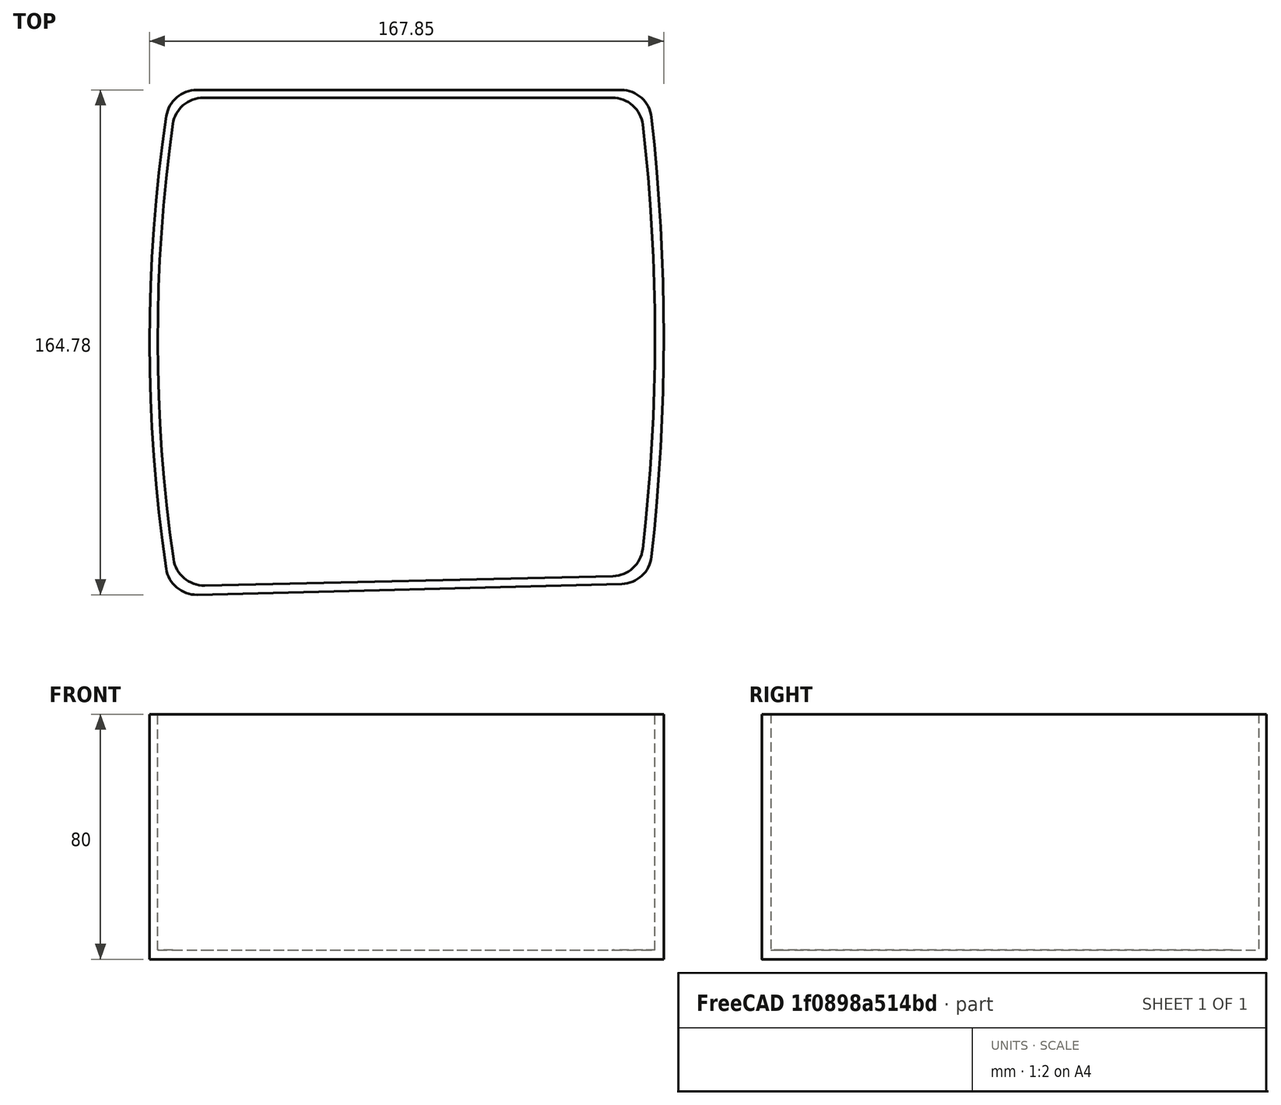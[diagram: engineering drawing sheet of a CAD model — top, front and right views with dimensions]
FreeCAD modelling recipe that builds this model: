
FCSTD DOCUMENT  (FreeCAD 0.19R)
Label: Milk
License: All rights reserved
LicenseURL: http://en.wikipedia.org/wiki/All_rights_reserved
objects: Sketcher::SketchObject×2, PartDesign::Fillet×2, PartDesign::Pad×1, PartDesign::Pocket×1, PartDesign::Body×1, Mesh::Feature×1
note: 11 computed .brp shape members not serialized (recipe doc carries the construction recipe); baked Part::Feature solids carry a one-line shape summary decoded from their .brp

FEATURE [Sketcher::SketchObject] Sketch
  FullyConstrained = false
  MapMode = 5
  Support = -> [XY_Plane]
  sketch-geometry (5):
    g0: ArcOfCircle CenterX=-567.525 CenterY=0 CenterZ=0 NormalX=0 NormalY=0 NormalZ=1 AngleXU=0 Radius=650.525 StartAngle=6.15912 EndAngle=6.40725
    g1: LineSegment StartX=-78 StartY=80.5 StartZ=0 EndX=78 EndY=80.5 EndZ=0
    g2: LineSegment StartX=-78 StartY=-84.5 StartZ=0 EndX=78 EndY=-80.5 EndZ=0
    g3: LineSegment StartX=83 StartY=48.8324 StartZ=0 EndX=83 EndY=-50.184 EndZ=0
    g4: ArcOfCircle CenterX=415.147 CenterY=-2 CenterZ=0 NormalX=0 NormalY=0 NormalZ=1 AngleXU=0 Radius=500 StartAngle=2.97583 EndAngle=3.30735
  constraints (15):
    c: PointOnObject(g0,g-1)
    c: Coincident(g1,g0)
    c: Coincident(g2,g0)
    c: Symmetric(g0,g1,g-2)
    c: Distance(g1) = 156
    c: Vertical(g3)
    c: Tangent(g3,g0)
    c: DistanceX(g0,g3) = 5
    c: DistanceY(g1) = 80.5
    c: DistanceY(g0) = -80.5
    c: DistanceY(g2) = -84.5
    c: DistanceX(g2) = -78
    c: Coincident(g4,g1)
    c: Coincident(g4,g2)
    c: Radius(g4) = 500
FEATURE [PartDesign::Pad] Pad
  Direction = (1,1,1)
  Length = 80
  Length2 = 100
  Profile = -> Sketch
  Type = 0
FEATURE [Sketcher::SketchObject] Sketch001
  FullyConstrained = false
  MapMode = 5
  Placement = pos=(0,0,80) rot=(0,0,1;0rad)
  Support = -> [Pad]
  sketch-geometry (4):
    g0: LineSegment StartX=-75.6334 StartY=-81.4504 StartZ=0 EndX=75.0731 EndY=-78 EndZ=0
    g1: LineSegment StartX=-75.9147 StartY=78 StartZ=0 EndX=75.0731 EndY=78 EndZ=0
    g2: ArcOfCircle CenterX=-519.835 CenterY=0 CenterZ=0 NormalX=0 NormalY=0 NormalZ=1 AngleXU=0 Radius=600 StartAngle=6.15282 EndAngle=6.41355
    g3: ArcOfCircle CenterX=417.828 CenterY=-0.854359 CenterZ=0 NormalX=0 NormalY=0 NormalZ=1 AngleXU=0 Radius=500 StartAngle=2.98322 EndAngle=3.30349
  constraints (11):
    c: PointOnObject(g2,g-1)
    c: Coincident(g2,g1)
    c: Coincident(g2,g0)
    c: DistanceY(g1) = 78
    c: DistanceY(g0) = -78
    c: Radius(g2) = 600
    c: Coincident(g3,g1)
    c: Coincident(g3,g0)
    c: Radius(g3) = 500
    c: DistanceX(g0) = -75.6334
    c: DistanceY(g0) = -81.4504
FEATURE [PartDesign::Pocket] Pocket
  BaseFeature = -> Pad
  Length = 77
  Length2 = 100
  Profile = -> Sketch001
  Type = 0
FEATURE [PartDesign::Fillet] Fillet
  Base = -> Pocket [Edge17,Edge22,Edge18,Edge20]
  BaseFeature = -> Pocket
  Radius = 10
  SupportTransform = false
FEATURE [PartDesign::Fillet] Fillet001
  Base = -> Fillet [Edge30,Edge29,Edge34,Edge32]
  BaseFeature = -> Fillet
  Radius = 10
  SupportTransform = false
FEATURE [PartDesign::Body] Body
  Group = -> [Sketch,Pad,Sketch001,Pocket,Fillet,Fillet001]
  Origin = -> Origin
  Tip = -> Fillet001
FEATURE [Mesh::Feature] Mesh  label="Fillet001 (Meshed)"
